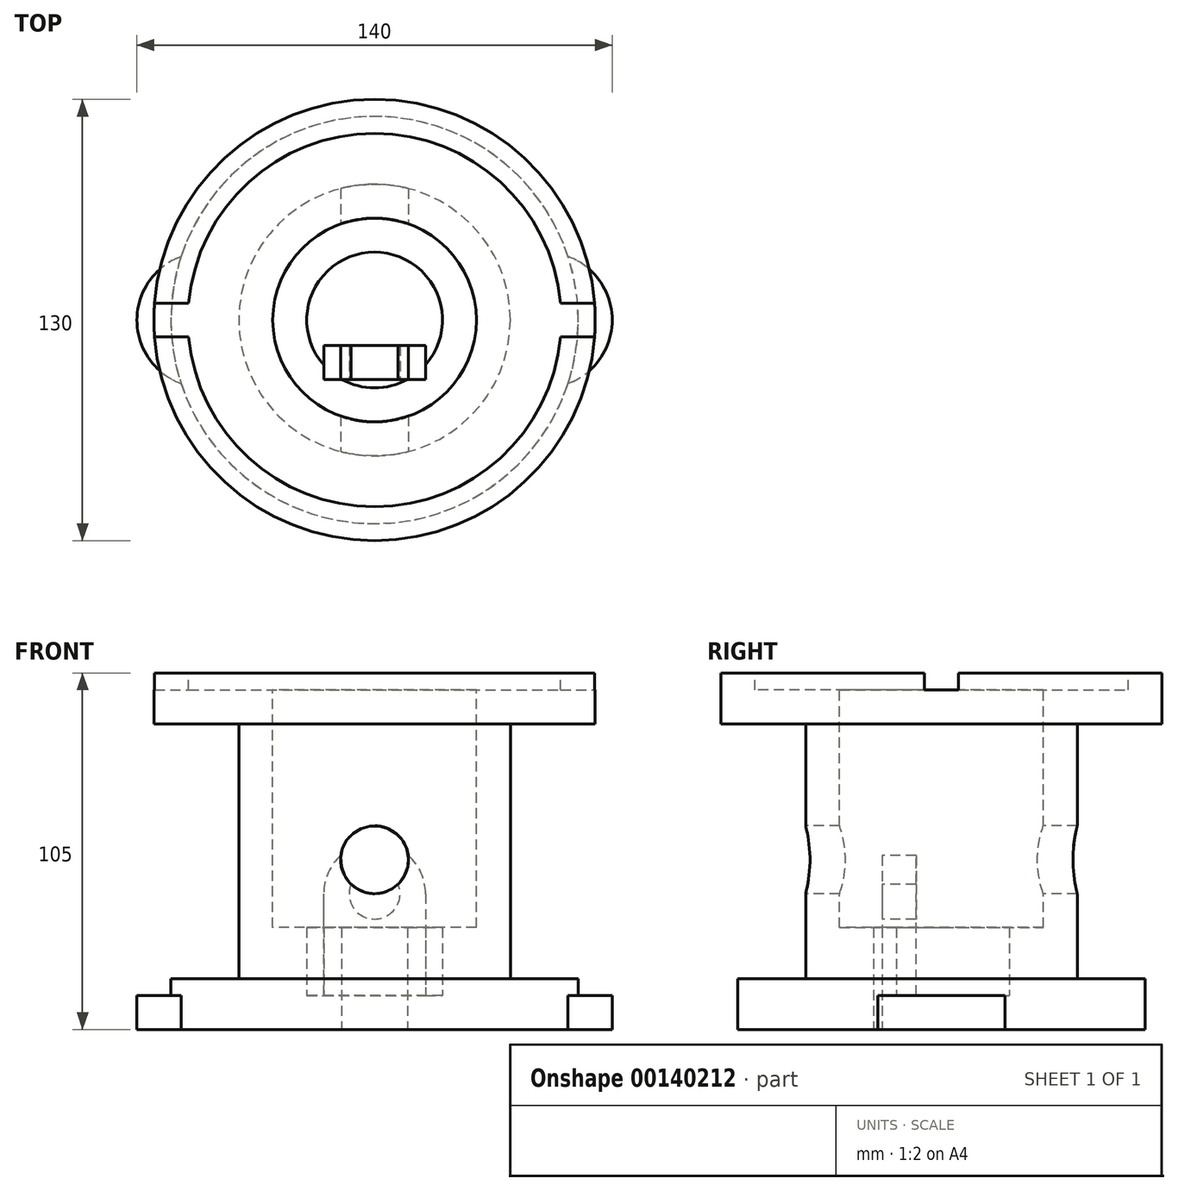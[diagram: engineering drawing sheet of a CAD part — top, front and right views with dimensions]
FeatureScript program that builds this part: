
annotation { "Feature Type Name" : "Feature", "Feature Type Description" : "" }
export const myFeature = defineFeature(function(context is Context, id is Id, definition is map)
    precondition{}
    {
        {
            var Q0;
            Q0=qCreatedBy(makeId("Top.planeOp"),FACE);
            var sketch = newSketch(context, id + "F0", { "sketchPlane" : qUnion([Q0])});
            skLineSegment(sketch, "E0.bottom", {"start": v(-35, -17.5) * mm, "end": v(35, -17.5) * mm});
            skLineSegment(sketch, "E0.top", {"start": v(-35, 17.5) * mm, "end": v(35, 17.5) * mm});
            skLineSegment(sketch, "E0.left", {"start": v(-35, -17.5) * mm, "end": v(-35, 17.5) * mm});
            skLineSegment(sketch, "E0.right", {"start": v(35, -17.5) * mm, "end": v(35, 17.5) * mm});
            skPoint(sketch, "E0.middle", {"position": v(0, 0) * mm});
            skSolve(sketch);
        }
        {
            var Q0;
            Q0=makeQuery(id+"F0.imprint","IMPRINT",FACE,{"disambiguationData":[TD([[makeQuery(id+"F0.imprint","IMPRINT",EDGE,{"derivedFrom":sQuery(id+"F0.wireOp",EDGE,"E0.bottom")}),1.0]])]});
            extrude(context, id + "F1", {"entities" : qUnion([Q0]), "depth" : 10 * mm});
        }
        {
            var Q0;
            Q0=makeQuery(id+"F1.opExtrude","SWEPT_FACE",FACE,{"disambiguationData":[OSD([sQuery(id+"F0.wireOp",EDGE,"E0.bottom")])]});
            var sketch = newSketch(context, id + "F2", { "sketchPlane" : qUnion([Q0])});
            skLineSegment(sketch, "E1", {"start": v(-15, 0) * mm, "end": v(-15, 40) * mm});
            skArc(sketch, "E2", {"start": v(15, 40) * mm, "mid": v(0, 55) * mm, "end": v(-15, 40) * mm});
            skLineSegment(sketch, "E3", {"start": v(15, 40) * mm, "end": v(15, 0) * mm});
            skLineSegment(sketch, "E4", {"start": v(-15, 0) * mm, "end": v(15, 0) * mm});
            skLineSegment(sketch, "E5", {"start": v(0, 0) * mm, "end": v(0, 40) * mm, "construction": true});
            skSolve(sketch);
        }
        {
            var Q0;
            {var subQ0=sQuery(id+"F2.wireOp",EDGE,"E2");Q0=makeQuery(id+"F2.imprint","IMPRINT",FACE,{"disambiguationData":[TD([[makeQuery(id+"F2.imprint","IMPRINT",EDGE,{"derivedFrom":subQ0}),1.0]])]});}
            extrude(context, id + "F3", {"entities" : qUnion([Q0]), "operationType" : NewBodyOperationType.ADD, "oppositeDirection" : true, "depth" : 10 * mm});
        }
        {
            var Q0;
            Q0=makeQuery(id+"F1.opExtrude","SWEPT_EDGE",EDGE,{"disambiguationData":[OSD([sQuery(id+"F0.wireOp",EDGE,"E0.bottom"),sQuery(id+"F0.wireOp",EDGE,"E0.left")])]});
            var Q1;
            Q1=makeQuery(id+"F1.opExtrude","SWEPT_EDGE",EDGE,{"disambiguationData":[OSD([sQuery(id+"F0.wireOp",EDGE,"E0.bottom"),sQuery(id+"F0.wireOp",EDGE,"E0.right")])]});
            var Q2;
            Q2=makeQuery(id+"F1.opExtrude","SWEPT_EDGE",EDGE,{"disambiguationData":[OSD([sQuery(id+"F0.wireOp",EDGE,"E0.top"),sQuery(id+"F0.wireOp",EDGE,"E0.right")])]});
            var Q3;
            Q3=makeQuery(id+"F1.opExtrude","SWEPT_EDGE",EDGE,{"disambiguationData":[OSD([sQuery(id+"F0.wireOp",EDGE,"E0.top"),sQuery(id+"F0.wireOp",EDGE,"E0.left")])]});
            fillet(context, id + "F4", {"entities" : qUnion([Q0, Q1, Q2, Q3]), "radius" : 5 * mm, "tangentPropagation" : true, "allowEdgeOverflow" : false});
        }
        {
            var Q0;
            {var subQ0=sQuery(id+"F0.wireOp",EDGE,"E0.bottom");Q0=makeQuery(id+"F3.boolean.opBoolean","MERGE",FACE,{"derivedFrom":[makeQuery(id+"F1.opExtrude","SWEPT_FACE",FACE,{"disambiguationData":[OSD([subQ0])]}),makeQuery(id+"F3.opExtrude","CAP_FACE",FACE,{"disambiguationData":[OSD([subQ0,sQuery(id+"F2.wireOp",EDGE,"E1"),sQuery(id+"F2.wireOp",EDGE,"E2"),sQuery(id+"F2.wireOp",EDGE,"E3")])],"isStart":true})]});}
            var sketch = newSketch(context, id + "F5", { "sketchPlane" : qUnion([Q0])});
            skCircle(sketch, "E6", {"center": v(0, 40) * mm, "radius": 7.5 * mm});
            skSolve(sketch);
        }
        {
            var Q0;
            Q0=makeQuery(id+"F5.imprint","IMPRINT",FACE,{"disambiguationData":[TD([[makeQuery(id+"F5.imprint","IMPRINT",EDGE,{"derivedFrom":sQuery(id+"F5.wireOp",EDGE,"E6")}),1.0]])]});
            extrude(context, id + "F6", {"entities" : qUnion([Q0]), "operationType" : NewBodyOperationType.REMOVE, "oppositeDirection" : true, "depth" : 25 * mm});
        }
        {
            var Q0;
            Q0=makeQuery(id+"F1.opExtrude","CAP_FACE",FACE,{"disambiguationData":[OSD([sQuery(id+"F0.wireOp",EDGE,"E0.bottom"),sQuery(id+"F0.wireOp",EDGE,"E0.top"),sQuery(id+"F0.wireOp",EDGE,"E0.left"),sQuery(id+"F0.wireOp",EDGE,"E0.right")])],"isStart":false});
            var sketch = newSketch(context, id + "F7", { "sketchPlane" : qUnion([Q0])});
            skLineSegment(sketch, "E7", {"start": v(0, -39.06) * mm, "end": v(0, 42.24) * mm, "construction": true});
            skLineSegment(sketch, "E8", {"start": v(25, -7.5) * mm, "end": v(25, 7.5) * mm, "construction": true});
            skArc(sketch, "E9.0.startCap", {"start": v(28.5, -7.5) * mm, "mid": v(25, -11) * mm, "end": v(21.5, -7.5) * mm});
            skArc(sketch, "E9.0.endCap", {"start": v(21.5, 7.5) * mm, "mid": v(25, 11) * mm, "end": v(28.5, 7.5) * mm});
            skLineSegment(sketch, "E9.0.left", {"start": v(21.5, -7.5) * mm, "end": v(21.5, 7.5) * mm});
            skLineSegment(sketch, "E9.0.right", {"start": v(28.5, -7.5) * mm, "end": v(28.5, 7.5) * mm});
            skArc(sketch, "E10.MirrorCS", {"start": v(-28.5, -7.5) * mm, "mid": v(-25, -11) * mm, "end": v(-21.5, -7.5) * mm});
            skLineSegment(sketch, "E11.MirrorCS", {"start": v(-21.5, -7.5) * mm, "end": v(-21.5, 7.5) * mm});
            skArc(sketch, "E12.MirrorCS", {"start": v(-21.5, 7.5) * mm, "mid": v(-25, 11) * mm, "end": v(-28.5, 7.5) * mm});
            skLineSegment(sketch, "E13.MirrorCS", {"start": v(-28.5, -7.5) * mm, "end": v(-28.5, 7.5) * mm});
            skSolve(sketch);
        }
        {
            var Q0;
            Q0 = qSketchRegion(id + "F7", true);
            extrude(context, id + "F8", {"entities" : qUnion([Q0]), "operationType" : NewBodyOperationType.REMOVE, "endBound" : BoundingType.THROUGH_ALL, "oppositeDirection" : true, "depth" : 25 * mm});
        }
        {
            var Q0;
            Q0=qCreatedBy(makeId("Front.planeOp"),FACE);
            var sketch = newSketch(context, id + "F9", { "sketchPlane" : qUnion([Q0])});
            skLineSegment(sketch, "E14", {"start": v(0, 134.8) * mm, "end": v(0, -122.9) * mm, "construction": true});
            skLineSegment(sketch, "E15", {"start": v(-146.6, 0) * mm, "end": v(147.79, 0) * mm, "construction": true});
            skLineSegment(sketch, "E16", {"start": v(-60, 0) * mm, "end": v(-30, 0) * mm});
            skLineSegment(sketch, "E17", {"start": v(-30, 0) * mm, "end": v(-30, 100) * mm});
            skLineSegment(sketch, "E18", {"start": v(-30, 100) * mm, "end": v(-55, 100) * mm});
            skLineSegment(sketch, "E19", {"start": v(-55, 100) * mm, "end": v(-55, 105) * mm});
            skLineSegment(sketch, "E20", {"start": v(-55, 105) * mm, "end": v(-65, 105) * mm});
            skLineSegment(sketch, "E21", {"start": v(-65, 105) * mm, "end": v(-65, 90) * mm});
            skLineSegment(sketch, "E22", {"start": v(-65, 90) * mm, "end": v(-40, 90) * mm});
            skLineSegment(sketch, "E23", {"start": v(-40, 90) * mm, "end": v(-40, 15) * mm});
            skLineSegment(sketch, "E24", {"start": v(-40, 15) * mm, "end": v(-60, 15) * mm});
            skLineSegment(sketch, "E25", {"start": v(-60, 15) * mm, "end": v(-60, 0) * mm});
            skSolve(sketch);
        }
        {
            var Q0;
            Q0=makeQuery(id+"F9.imprint","IMPRINT",FACE,{"disambiguationData":[TD([[makeQuery(id+"F9.imprint","IMPRINT",EDGE,{"derivedFrom":sQuery(id+"F9.wireOp",EDGE,"E16")}),1.0]])]});
            var Q1;
            Q1=sQuery(id+"F9.wireOp",EDGE,"E14");
            revolve(context, id + "F10", {"entities" : qUnion([Q0]), "axis" : qUnion([Q1]), "revolveType" : RevolveType.FULL});
        }
        {
            var Q0;
            Q0=qCreatedBy(makeId("Front.planeOp"),FACE);
            var sketch = newSketch(context, id + "F11", { "sketchPlane" : qUnion([Q0])});
            skCircle(sketch, "E26", {"center": v(0, 50) * mm, "radius": 10 * mm});
            skSolve(sketch);
        }
        {
            var Q0;
            Q0 = qSketchRegion(id + "F11", true);
            extrude(context, id + "F12", {"entities" : qUnion([Q0]), "operationType" : NewBodyOperationType.REMOVE, "endBound" : BoundingType.THROUGH_ALL, "oppositeDirection" : true, "depth" : 25 * mm, "hasSecondDirection" : true, "secondDirectionBound" : SecondDirectionBoundingType.THROUGH_ALL, "secondDirectionOppositeDirection" : false, "secondDirectionDepth" : 25 * mm});
        }
        {
            var Q0;
            Q0=qCreatedBy(makeId("Right.planeOp"),FACE);
            var sketch = newSketch(context, id + "F13", { "sketchPlane" : qUnion([Q0])});
            skLineSegment(sketch, "E27.0.0", {"start": v(-55, 100) * mm, "end": v(55, 100) * mm, "construction": true});
            skLineSegment(sketch, "E28", {"start": v(0, 0) * mm, "end": v(0, 141.04) * mm, "construction": true});
            skPoint(sketch, "E28.endSnap0", {"position": v(0, 100) * mm});
            skLineSegment(sketch, "E29", {"start": v(-5, 100) * mm, "end": v(-5, 105) * mm});
            skLineSegment(sketch, "E30", {"start": v(-5, 105) * mm, "end": v(5, 105) * mm});
            skLineSegment(sketch, "E31", {"start": v(5, 105) * mm, "end": v(5, 100) * mm});
            skLineSegment(sketch, "E32", {"start": v(5, 100) * mm, "end": v(-5, 100) * mm});
            skSolve(sketch);
        }
        {
            var Q0;
            Q0=makeQuery(id+"F13.imprint","IMPRINT",FACE,{"disambiguationData":[TD([[makeQuery(id+"F13.imprint","IMPRINT",EDGE,{"derivedFrom":sQuery(id+"F13.wireOp",EDGE,"E29")}),-1.0]])]});
            extrude(context, id + "F14", {"entities" : qUnion([Q0]), "operationType" : NewBodyOperationType.REMOVE, "endBound" : BoundingType.THROUGH_ALL, "oppositeDirection" : true, "depth" : 25 * mm, "hasSecondDirection" : true, "secondDirectionBound" : SecondDirectionBoundingType.THROUGH_ALL, "secondDirectionOppositeDirection" : false, "secondDirectionDepth" : 25 * mm});
        }
        {
            var Q0;
            Q0=qCreatedBy(makeId("Top.planeOp"),FACE);
            var sketch = newSketch(context, id + "F15", { "sketchPlane" : qUnion([Q0])});
            skLineSegment(sketch, "E33", {"start": v(0, 61.26) * mm, "end": v(0, -62.36) * mm, "construction": true});
            skLineSegment(sketch, "E34", {"start": v(-104.49, 0) * mm, "end": v(100.97, 0) * mm, "construction": true});
            skArc(sketch, "E35", {"start": v(0, 40) * mm, "mid": v(-8.17, 39.16) * mm, "end": v(-16, 36.66) * mm});
            skArc(sketch, "E36", {"start": v(-58, 18.33) * mm, "mid": v(-70, 0) * mm, "end": v(-58, -18.33) * mm});
            skLineSegment(sketch, "E37", {"start": v(-58, 18.33) * mm, "end": v(-16, 36.66) * mm});
            skLineSegment(sketch, "E38", {"start": v(-58, -18.33) * mm, "end": v(-16, -36.66) * mm});
            skArc(sketch, "E39.trimOffspring", {"start": v(-16, -36.66) * mm, "mid": v(-8.17, -39.16) * mm, "end": v(0, -40) * mm});
            skArc(sketch, "E40.MirrorCS", {"start": v(0, 40) * mm, "mid": v(8.17, 39.16) * mm, "end": v(16, 36.66) * mm});
            skLineSegment(sketch, "E41.MirrorCS", {"start": v(58, 18.33) * mm, "end": v(16, 36.66) * mm});
            skArc(sketch, "E42.MirrorCS", {"start": v(58, 18.33) * mm, "mid": v(70, 0) * mm, "end": v(58, -18.33) * mm});
            skLineSegment(sketch, "E43.MirrorCS", {"start": v(58, -18.33) * mm, "end": v(16, -36.66) * mm});
            skArc(sketch, "E44.MirrorCS", {"start": v(16, -36.66) * mm, "mid": v(8.17, -39.16) * mm, "end": v(0, -40) * mm});
            skCircle(sketch, "E45", {"center": v(-50, 0) * mm, "radius": 7.5 * mm});
            skCircle(sketch, "E46", {"center": v(50, 0) * mm, "radius": 7.5 * mm});
            skSolve(sketch);
        }
        {
            var Q0;
            Q0=makeQuery(id+"F15.imprint","IMPRINT",FACE,{"disambiguationData":[TD([[makeQuery(id+"F15.imprint","IMPRINT",EDGE,{"derivedFrom":sQuery(id+"F15.wireOp",EDGE,"E35")}),1.0]])]});
            extrude(context, id + "F16", {"entities" : qUnion([Q0]), "depth" : 10 * mm});
        }
        {
            var Q0;
            Q0=makeQuery(id+"F16.opExtrude","CAP_FACE",FACE,{"disambiguationData":[OSD([sQuery(id+"F15.wireOp",EDGE,"E35"),sQuery(id+"F15.wireOp",EDGE,"E36"),sQuery(id+"F15.wireOp",EDGE,"E37"),sQuery(id+"F15.wireOp",EDGE,"E38"),sQuery(id+"F15.wireOp",EDGE,"E39.trimOffspring"),sQuery(id+"F15.wireOp",EDGE,"E40.MirrorCS"),sQuery(id+"F15.wireOp",EDGE,"E41.MirrorCS"),sQuery(id+"F15.wireOp",EDGE,"E42.MirrorCS"),sQuery(id+"F15.wireOp",EDGE,"E43.MirrorCS"),sQuery(id+"F15.wireOp",EDGE,"E44.MirrorCS"),sQuery(id+"F15.wireOp",EDGE,"E45"),sQuery(id+"F15.wireOp",EDGE,"E46")])],"isStart":false});
            var sketch = newSketch(context, id + "F17", { "sketchPlane" : qUnion([Q0])});
            skCircle(sketch, "E47", {"center": v(0, 0) * mm, "radius": 30 * mm});
            skCircle(sketch, "E48", {"center": v(0, 0) * mm, "radius": 20 * mm});
            skSolve(sketch);
        }
        {
            var Q0;
            Q0=makeQuery(id+"F17.imprint","IMPRINT",FACE,{"disambiguationData":[TD([[makeQuery(id+"F17.imprint","IMPRINT",EDGE,{"derivedFrom":sQuery(id+"F17.wireOp",EDGE,"E47")}),1.0]])]});
            extrude(context, id + "F18", {"entities" : qUnion([Q0]), "operationType" : NewBodyOperationType.ADD, "depth" : 20 * mm});
        }
        {
            var Q0;
            Q0=makeQuery(id+"F18.boolean.opBoolean","SPLIT",FACE,{"disambiguationData":[TD([makeQuery(id+"F18.opExtrude","SWEPT_FACE",FACE,{"disambiguationData":[OSD([sQuery(id+"F17.wireOp",EDGE,"E48")])]})])],"derivedFrom":makeQuery(id+"F16.opExtrude","CAP_FACE",FACE,{"disambiguationData":[OSD([sQuery(id+"F15.wireOp",EDGE,"E35"),sQuery(id+"F15.wireOp",EDGE,"E36"),sQuery(id+"F15.wireOp",EDGE,"E37"),sQuery(id+"F15.wireOp",EDGE,"E38"),sQuery(id+"F15.wireOp",EDGE,"E39.trimOffspring"),sQuery(id+"F15.wireOp",EDGE,"E40.MirrorCS"),sQuery(id+"F15.wireOp",EDGE,"E41.MirrorCS"),sQuery(id+"F15.wireOp",EDGE,"E42.MirrorCS"),sQuery(id+"F15.wireOp",EDGE,"E43.MirrorCS"),sQuery(id+"F15.wireOp",EDGE,"E44.MirrorCS"),sQuery(id+"F15.wireOp",EDGE,"E45"),sQuery(id+"F15.wireOp",EDGE,"E46")])],"isStart":false})});
            extrude(context, id + "F19", {"entities" : qUnion([Q0]), "operationType" : NewBodyOperationType.REMOVE, "endBound" : BoundingType.THROUGH_ALL, "oppositeDirection" : true, "depth" : 25 * mm});
        }
    });
